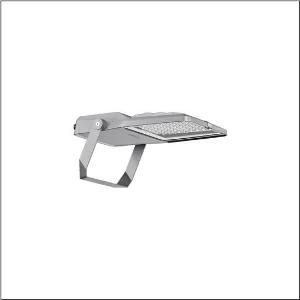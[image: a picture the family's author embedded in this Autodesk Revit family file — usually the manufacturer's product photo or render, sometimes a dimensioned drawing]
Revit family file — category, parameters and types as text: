
# Revit family: floodlight_fl_21_iq_mini___pl33t_5xa7772b5f1a_9cd7
name_source: partatom
category: Lighting Fixtures
units: mm (PartAtom-declared; Revit-internal decimal feet)

## family parameters
Cut with Voids When Loaded = No
Host = Face
Light Source = No
Part Type = Normal
Room Calculation Point = No
Round Connector Dimension = Use Diameter
Shared = No

## types (1)
- --- (1 x LED, 5750 lm, 45.5 W, 4000K)
    Apparent Load = 46 VA
    CIE Flux Codes = 26 75 99 100 100
    Color Rendering = 80
    Color Temperature = 4000K
    Default Elevation = 1800 mm
    Description = Floodlight FL 21 iQ mini, floodlight, primary light control with lens, of PMMA, primary optical cover: protective disc, of toughened safety glass, transparent, light distribution: PL33T, light emission: direct distribution, installation type: surface-mounted, LED, High Power LED, rated luminous flux: 5.750lm, luminous efficacy: 126lm/W, light colour: 840, colour temperature: 4000K, control: Street-Remote, Auto-Match, Temp-Guard, Night-Set, Smart-Wire, Desk-Remote (wireless, voltage-free reading and setting of iQ features in the workshop via application-optimized NFC function/RFID function), optimised constant luminous flux control (CLO 2.0), with terminal, 6-pole, mains connection: 220..240V, AC, 50/60Hz, start of lifetime: 46W, end of service life: 48W, reduction: 22W, luminaire housing, of diecast aluminium, powder-coated, Siteco® metallic grey (DB 702S), corrosivity category C5 mid according to DIN EN ISO 12944, sealing non-destructively replaceable, mounting bracket, of steel, galvanised, powder-coated, Siteco® metallic grey (DB 702S), protection rating (complete): IP66, insulation class (complete): insulation class II (safety insulation), certification: CE, ENEC, VDE, protection symbol: D, impact resistance: IK08, permissible operating ambient temperature: -40..+40°C, permissible operating ambient temperature for outdoor applications: -40..+50°C, standard: DIN EN 12944, LABS conformity tested according to VDMA 24364:2018-05, packaging unit: 1 piece

Light Distribution: PL33T
    Height = 70 mm
    Lamp = 1 x LED
    Lamp Light Flux = 5750 lm
    Lamp Power = 45.5 W
    Lamp count = 1
    Length = 485 mm
    Luminous efficacy = 126 lm/W
    Manufacturer = Siteco
    ModVariant = No
    Model = 5XA7772B5F1A
    Number of Poles = 1
    OnlyDefault = Yes
    Power Factor = 1
    Product Name = Floodlight FL 21 iQ mini | PL33T
    Product group = floodlight | pylon annexe
    ProductGroupID = 6200
    Protection Class = Protection class II
    Protection Degree = IP 66
    RLX_Detail_Level = 1
    RLX_Emergency_Light_Flux = 0 lm
    RLX_Emergency_Type = 0
    RLX_Emergency_Type_DB = No
    RlxData = <blob elided: 96113 chars, md5=1ab689c3>
    Socket = socket
    Standby Power = 0 W
    System Light Flux = 5750 lm
    System Power = 46 W
    Type Comments = factory setting: luminous flux: 100 % | dim-lin: 254 | 463 mA
    Type Image = l_1006845.jpg
    URL = http://relux.com
    VarID = @adj_100009
    Voltage = 0 V
    Weight = 0.00 kg
    Width = 337 mm

## geometry (parser evidence)
native form markers: Blend x4, Sweep x11
no freeform markers — native parametric forms only
